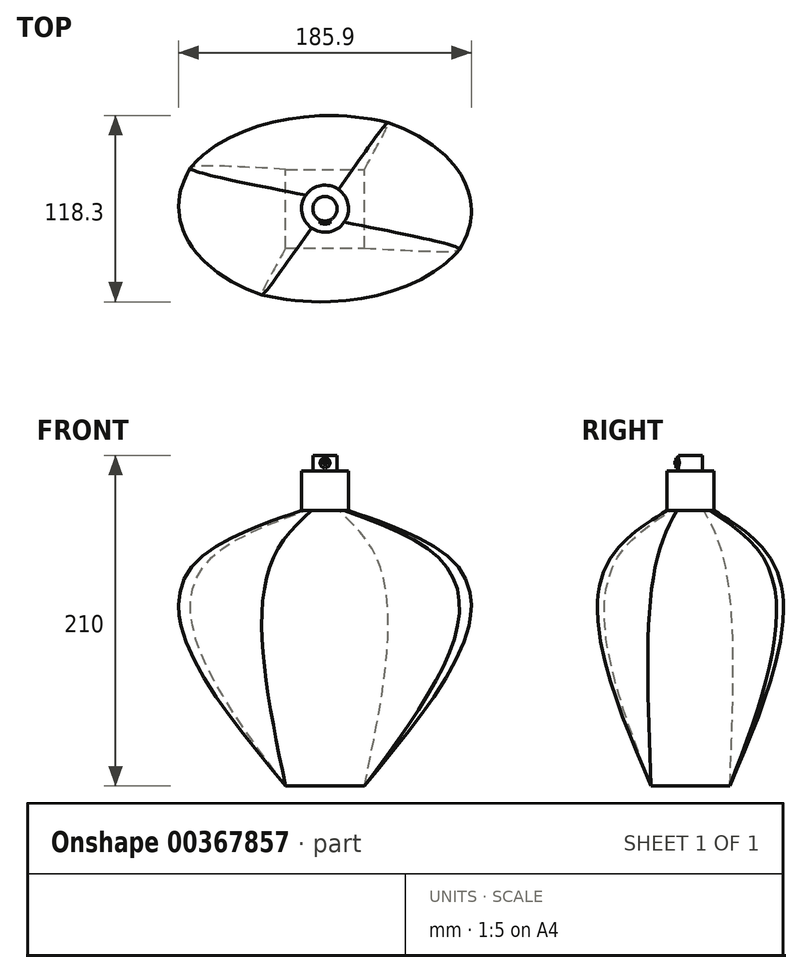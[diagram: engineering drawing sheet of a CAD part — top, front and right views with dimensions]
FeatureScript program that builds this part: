
annotation { "Feature Type Name" : "Feature", "Feature Type Description" : "" }
export const myFeature = defineFeature(function(context is Context, id is Id, definition is map)
    precondition{}
    {
        {
            var Q0;
            Q0=qCreatedBy(makeId("Top.planeOp"),FACE);
            var sketch = newSketch(context, id + "F0", { "sketchPlane" : qUnion([Q0])});
            skLineSegment(sketch, "E0.bottom", {"start": v(-25, -25) * mm, "end": v(25, -25) * mm});
            skLineSegment(sketch, "E0.top", {"start": v(-25, 25) * mm, "end": v(25, 25) * mm});
            skLineSegment(sketch, "E0.left", {"start": v(-25, -25) * mm, "end": v(-25, 25) * mm});
            skLineSegment(sketch, "E0.right", {"start": v(25, -25) * mm, "end": v(25, 25) * mm});
            skPoint(sketch, "E0.middle", {"position": v(0, 0) * mm});
            skSolve(sketch);
        }
        {
            var Q0;
            Q0=qCreatedBy(makeId("Top.planeOp"),FACE);
            cPlane(context, id + "F1", {"entities" : qUnion([Q0]), "cplaneType" : CPlaneType.OFFSET, "offset" : 150 * mm, "width" : 150 * mm, "height" : 150 * mm});
        }
        {
            var Q0;
            Q0=qCreatedBy(id+"F1.planeOp",FACE);
            var sketch = newSketch(context, id + "F2", { "sketchPlane" : qUnion([Q0])});
            skEllipse(sketch, "E1", {"center": v(0, 0) * mm, "majorRadius": 72.76 * mm, "minorRadius": 47.12 * mm, "majorAxis": v(-1, 0)});
            skSolve(sketch);
        }
        {
            var Q0;
            Q0=qCreatedBy(id+"F1.planeOp",FACE);
            cPlane(context, id + "F3", {"entities" : qUnion([Q0]), "cplaneType" : CPlaneType.OFFSET, "offset" : 25 * mm, "width" : 150 * mm, "height" : 150 * mm});
        }
        {
            var Q0;
            Q0=qCreatedBy(id+"F3.planeOp",FACE);
            var sketch = newSketch(context, id + "F4", { "sketchPlane" : qUnion([Q0])});
            skCircle(sketch, "E2", {"center": v(0, 0) * mm, "radius": 14.93 * mm});
            skSolve(sketch);
        }
        {
            var Q0;
            Q0=makeQuery(id+"F0.imprint","IMPRINT",FACE,{"disambiguationData":[TD([[makeQuery(id+"F0.imprint","IMPRINT",EDGE,{"derivedFrom":sQuery(id+"F0.wireOp",EDGE,"E0.bottom")}),1.0]])]});
            var Q1;
            Q1=makeQuery(id+"F2.imprint","IMPRINT",FACE,{"disambiguationData":[TD([[makeQuery(id+"F2.imprint","IMPRINT",EDGE,{"derivedFrom":sQuery(id+"F2.wireOp",EDGE,"E1")}),1.0]])]});
            var Q2;
            Q2=makeQuery(id+"F4.imprint","IMPRINT",FACE,{"disambiguationData":[TD([[makeQuery(id+"F4.imprint","IMPRINT",EDGE,{"derivedFrom":sQuery(id+"F4.wireOp",EDGE,"E2")}),1.0]])]});
            loft(context, id + "F5", {"sheetProfilesArray" : [{ "sheetProfileEntities" : qUnion([Q0]) }, { "sheetProfileEntities" : qUnion([Q1]) }, { "sheetProfileEntities" : qUnion([Q2]) }]});
        }
        {
            var Q0;
            Q0=makeQuery(id+"F5.opLoft","CAP_FACE",FACE,{"disambiguationData":[OSD([makeQuery(id+"F4.imprint","IMPRINT",FACE,{"disambiguationData":[TD([[makeQuery(id+"F4.imprint","IMPRINT",EDGE,{"derivedFrom":sQuery(id+"F4.wireOp",EDGE,"E2")}),1.0]])]})])],"isStart":true});
            extrude(context, id + "F6", {"entities" : qUnion([Q0]), "operationType" : NewBodyOperationType.ADD, "depth" : 25 * mm});
        }
        {
            var Q0;
            Q0=qCreatedBy(id+"F3.planeOp",FACE);
            cPlane(context, id + "F7", {"entities" : qUnion([Q0]), "cplaneType" : CPlaneType.OFFSET, "offset" : 25 * mm, "width" : 150 * mm, "height" : 150 * mm});
        }
        {
            var Q0;
            Q0=qCreatedBy(id+"F7.planeOp",FACE);
            var sketch = newSketch(context, id + "F8", { "sketchPlane" : qUnion([Q0])});
            skCircle(sketch, "E3", {"center": v(0, 0) * mm, "radius": 7.77 * mm});
            skSolve(sketch);
        }
        {
            var Q0;
            Q0=makeQuery(id+"F8.imprint","IMPRINT",FACE,{"disambiguationData":[TD([[makeQuery(id+"F8.imprint","IMPRINT",EDGE,{"derivedFrom":sQuery(id+"F8.wireOp",EDGE,"E3")}),1.0]])]});
            extrude(context, id + "F9", {"entities" : qUnion([Q0]), "operationType" : NewBodyOperationType.ADD, "depth" : 10 * mm});
        }
        {
            var Q0;
            Q0=qCreatedBy(makeId("Front.planeOp"),FACE);
            var sketch = newSketch(context, id + "F10", { "sketchPlane" : qUnion([Q0])});
            skCircle(sketch, "E4", {"center": v(0, 205.48) * mm, "radius": 2.4 * mm});
            skSolve(sketch);
        }
        {
            var Q0;
            Q0=sQuery(id+"F10.wireOp",EDGE,"E4");
            extrude(context, id + "F11", {"bodyType" : ToolBodyType.SURFACE, "surfaceEntities" : qUnion([Q0]), "depth" : 7 * mm});
        }
        {
            var Q0;
            Q0=qCreatedBy(makeId("Front.planeOp"),FACE);
            var sketch = newSketch(context, id + "F12", { "sketchPlane" : qUnion([Q0])});
            skCircle(sketch, "E5", {"center": v(0, 205.24) * mm, "radius": 3.13 * mm});
            skSolve(sketch);
        }
        {
            var Q0;
            Q0 = qSketchRegion(id + "F12", true);
            extrude(context, id + "F13", {"entities" : qUnion([Q0]), "operationType" : NewBodyOperationType.ADD, "depth" : 9.3 * mm});
        }
        {
            var Q0;
            Q0=makeQuery(id+"F13.opExtrude","CAP_FACE",FACE,{"disambiguationData":[OSD([sQuery(id+"F12.wireOp",EDGE,"E5")])],"isStart":false});
            var sketch = newSketch(context, id + "F14", { "sketchPlane" : qUnion([Q0])});
            skCircle(sketch, "E6", {"center": v(0, 205.24) * mm, "radius": 1.17 * mm});
            skSolve(sketch);
        }
        {
            var Q0;
            Q0=makeQuery(id+"F14.imprint","IMPRINT",FACE,{"disambiguationData":[TD([[makeQuery(id+"F14.imprint","IMPRINT",EDGE,{"derivedFrom":sQuery(id+"F14.wireOp",EDGE,"E6")}),1.0]])]});
            var Q1;
            Q1=sQuery(id+"F14.wireOp",EDGE,"E6");
            extrude(context, id + "F15", {"entities" : qUnion([Q0]), "operationType" : NewBodyOperationType.ADD, "surfaceEntities" : qUnion([Q1]), "depth" : 0.39 * mm});
        }
    });
